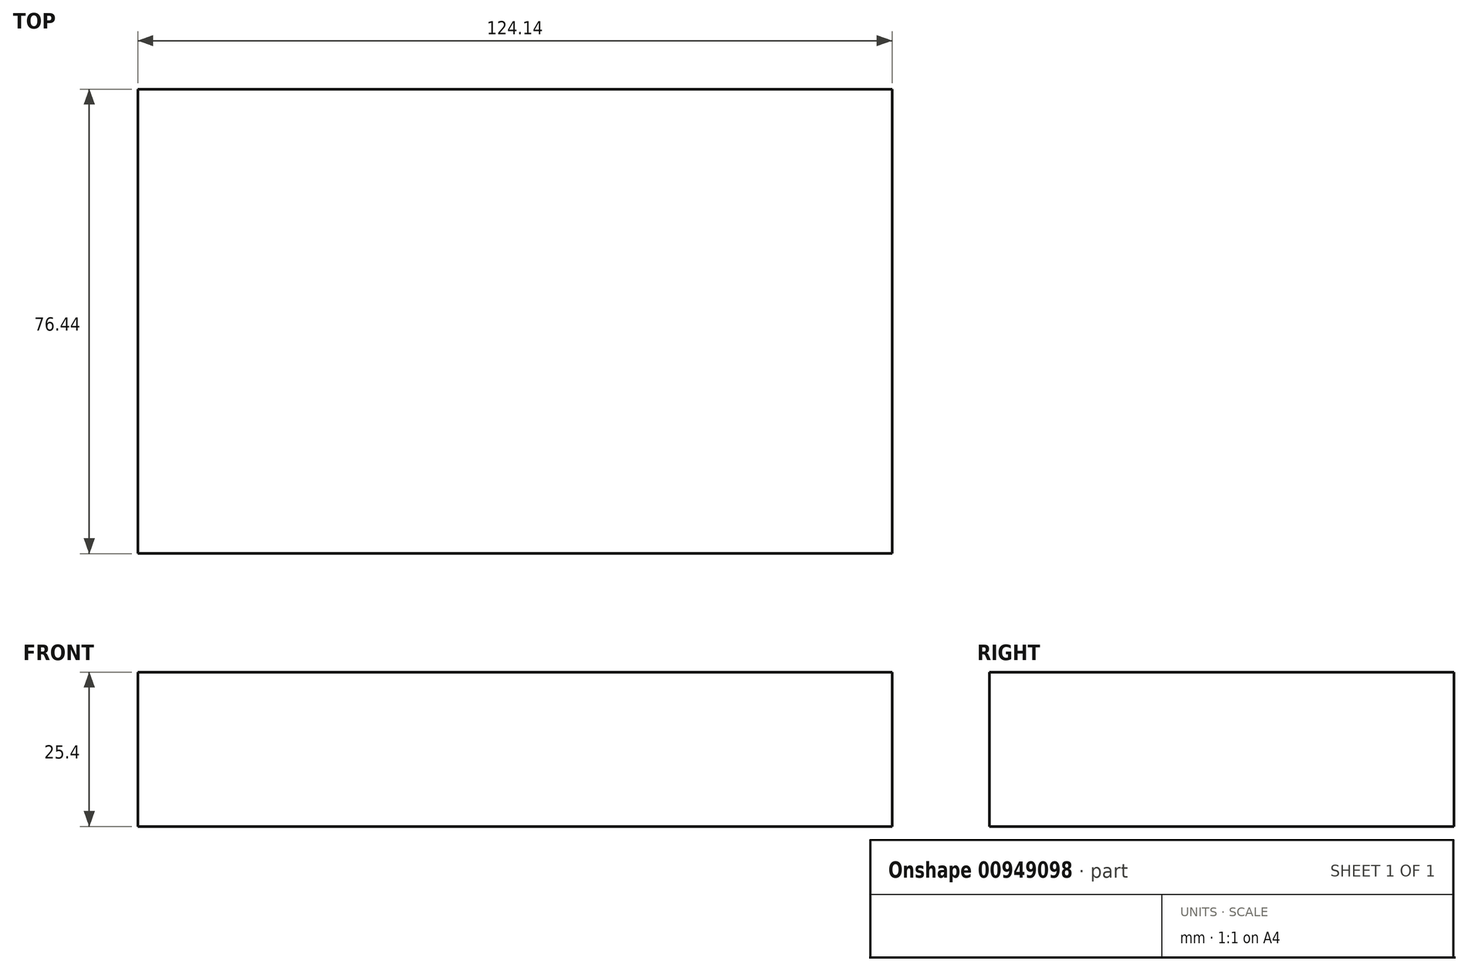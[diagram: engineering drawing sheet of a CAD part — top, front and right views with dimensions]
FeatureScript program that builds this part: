
annotation { "Feature Type Name" : "Feature", "Feature Type Description" : "" }
export const myFeature = defineFeature(function(context is Context, id is Id, definition is map)
    precondition{}
    {
        {
            var Q0;
            Q0=qCreatedBy(makeId("Top.planeOp"),FACE);
            var sketch = newSketch(context, id + "F0", { "sketchPlane" : qUnion([Q0])});
            skLineSegment(sketch, "E0.bottom", {"start": v(27.43, 0) * mm, "end": v(151.57, 0) * mm});
            skLineSegment(sketch, "E0.top", {"start": v(27.43, -76.44) * mm, "end": v(151.57, -76.44) * mm});
            skLineSegment(sketch, "E0.left", {"start": v(27.43, 0) * mm, "end": v(27.43, -76.44) * mm});
            skLineSegment(sketch, "E0.right", {"start": v(151.57, 0) * mm, "end": v(151.57, -76.44) * mm});
            skSolve(sketch);
        }
        {
            var Q0;
            Q0 = qSketchRegion(id + "F0", true);
            extrude(context, id + "F1", {"entities" : qUnion([Q0]), "depth" : 25.4 * mm, "offsetDistance" : 25.4 * mm});
        }
    });
